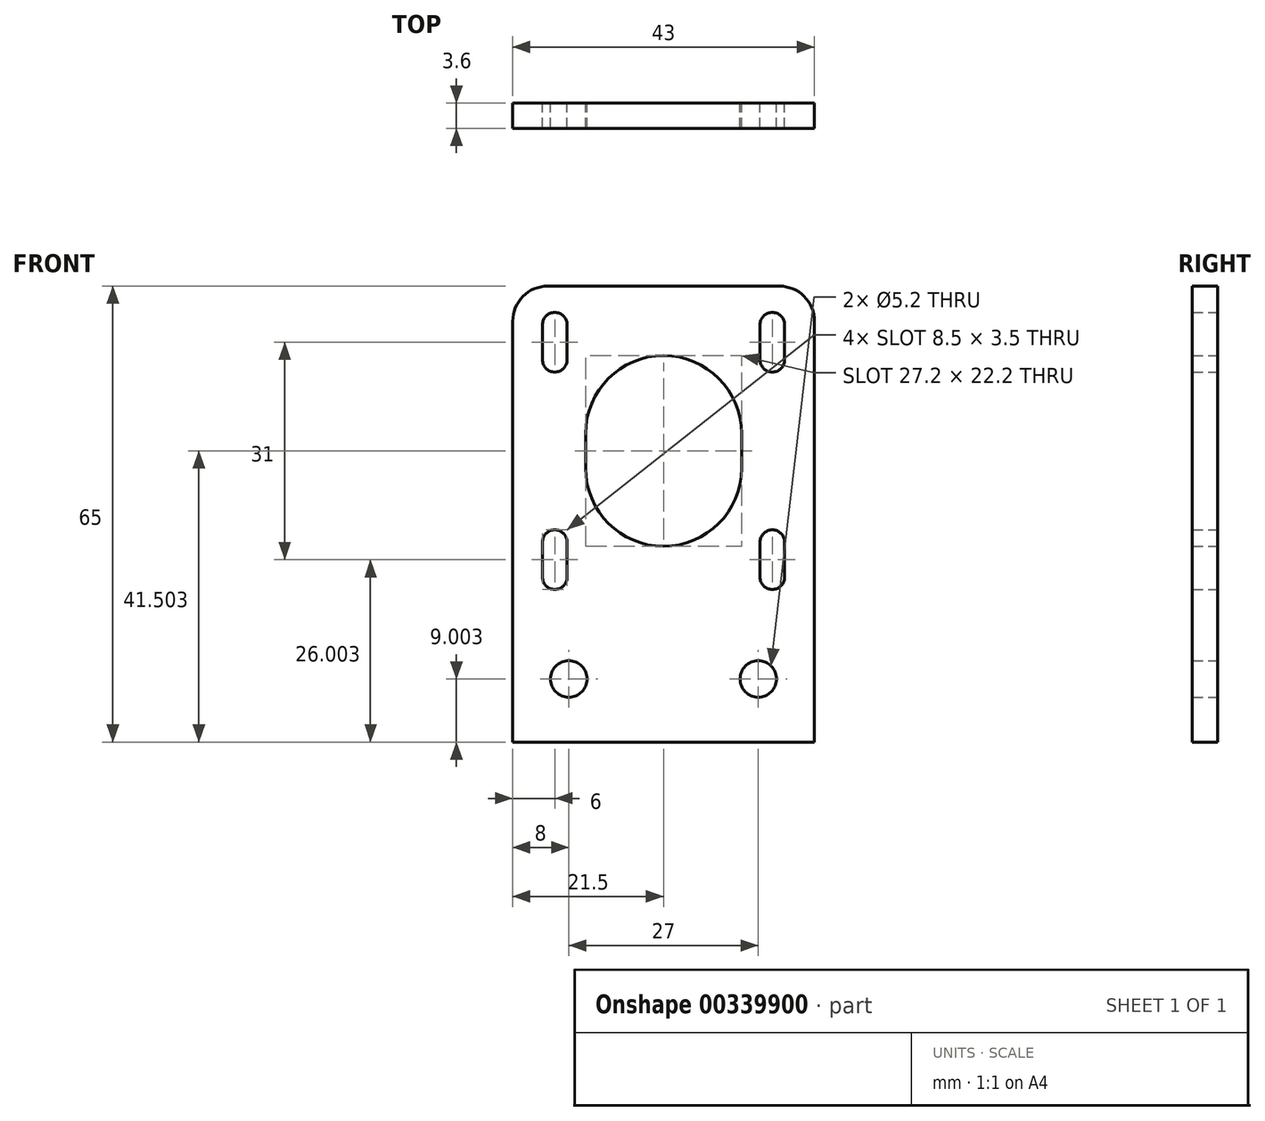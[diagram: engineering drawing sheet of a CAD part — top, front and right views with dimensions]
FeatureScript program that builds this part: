
annotation { "Feature Type Name" : "Feature", "Feature Type Description" : "" }
export const myFeature = defineFeature(function(context is Context, id is Id, definition is map)
    precondition{}
    {
        {
            var Q0;
            Q0=qCreatedBy(makeId("Front.planeOp"),FACE);
            var sketch = newSketch(context, id + "F0", { "sketchPlane" : qUnion([Q0])});
            skLineSegment(sketch, "E0.bottom", {"start": v(-21.5, 27.25) * mm, "end": v(21.5, 27.25) * mm});
            skLineSegment(sketch, "E0.top", {"start": v(-21.5, -37.75) * mm, "end": v(21.5, -37.75) * mm});
            skLineSegment(sketch, "E0.left", {"start": v(-21.5, 27.25) * mm, "end": v(-21.5, -37.75) * mm});
            skLineSegment(sketch, "E0.right", {"start": v(21.5, 27.25) * mm, "end": v(21.5, -37.75) * mm});
            skLineSegment(sketch, "E1", {"start": v(-21.5, -19.75) * mm, "end": v(21.5, -19.75) * mm, "construction": true});
            skLineSegment(sketch, "E2", {"start": v(-21.5, -28.75) * mm, "end": v(21.5, -28.75) * mm, "construction": true});
            skLineSegment(sketch, "E3", {"start": v(-21.5, 1.25) * mm, "end": v(21.5, 1.25) * mm, "construction": true});
            skPoint(sketch, "E3.endSnap0", {"position": v(21.5, -5.25) * mm});
            skLineSegment(sketch, "E4", {"start": v(-21.5, 6.25) * mm, "end": v(21.5, 6.25) * mm, "construction": true});
            skLineSegment(sketch, "E5", {"start": v(0, 27.25) * mm, "end": v(0, -37.75) * mm, "construction": true});
            skPoint(sketch, "E5.endSnap0", {"position": v(0, -37.75) * mm});
            skCircle(sketch, "E6", {"center": v(0, 1.25) * mm, "radius": 11.1 * mm});
            skCircle(sketch, "E7", {"center": v(0, 6.25) * mm, "radius": 11.1 * mm});
            skLineSegment(sketch, "E8", {"start": v(11.1, 1.25) * mm, "end": v(11.1, 6.25) * mm});
            skLineSegment(sketch, "E9", {"start": v(-11.1, 6.25) * mm, "end": v(-11.1, 1.25) * mm});
            skLineSegment(sketch, "E10", {"start": v(-15.5, 27.25) * mm, "end": v(-15.5, -19.75) * mm, "construction": true});
            skLineSegment(sketch, "E11", {"start": v(15.5, 27.25) * mm, "end": v(15.5, -19.75) * mm, "construction": true});
            skLineSegment(sketch, "E12", {"start": v(-21.5, -9.25) * mm, "end": v(21.5, -9.25) * mm, "construction": true});
            skLineSegment(sketch, "E13", {"start": v(-21.5, 21.75) * mm, "end": v(21.5, 21.75) * mm, "construction": true});
            skCircle(sketch, "E14", {"center": v(-15.5, 21.75) * mm, "radius": 1.75 * mm});
            skCircle(sketch, "E15", {"center": v(15.5, 21.75) * mm, "radius": 1.75 * mm});
            skCircle(sketch, "E16", {"center": v(-15.5, -9.25) * mm, "radius": 1.75 * mm});
            skCircle(sketch, "E17", {"center": v(15.5, -9.25) * mm, "radius": 1.75 * mm});
            skCircle(sketch, "E18", {"center": v(-15.5, 16.75) * mm, "radius": 1.75 * mm});
            skCircle(sketch, "E19", {"center": v(15.5, 16.75) * mm, "radius": 1.75 * mm});
            skCircle(sketch, "E20", {"center": v(15.5, -14.25) * mm, "radius": 1.75 * mm});
            skCircle(sketch, "E21", {"center": v(-15.5, -14.25) * mm, "radius": 1.75 * mm});
            skLineSegment(sketch, "E22", {"start": v(-17.25, 21.75) * mm, "end": v(-17.25, 16.75) * mm});
            skLineSegment(sketch, "E23", {"start": v(-13.75, 21.75) * mm, "end": v(-13.75, 16.75) * mm});
            skLineSegment(sketch, "E24", {"start": v(13.75, 21.75) * mm, "end": v(13.75, 16.75) * mm});
            skLineSegment(sketch, "E25", {"start": v(17.25, 21.75) * mm, "end": v(17.25, 16.75) * mm});
            skLineSegment(sketch, "E26", {"start": v(-17.25, -9.25) * mm, "end": v(-17.25, -14.25) * mm});
            skLineSegment(sketch, "E27", {"start": v(-13.75, -9.25) * mm, "end": v(-13.75, -14.25) * mm});
            skLineSegment(sketch, "E28", {"start": v(13.75, -9.25) * mm, "end": v(13.75, -14.25) * mm});
            skLineSegment(sketch, "E29", {"start": v(17.25, -9.25) * mm, "end": v(17.25, -14.25) * mm});
            skCircle(sketch, "E30", {"center": v(-13.5, -28.75) * mm, "radius": 2.6 * mm});
            skCircle(sketch, "E31", {"center": v(13.5, -28.75) * mm, "radius": 2.6 * mm});
            skSolve(sketch);
        }
        {
            var Q0;
            Q0 = qSketchRegion(id + "F0", true);
            extrude(context, id + "F1", {"entities" : qUnion([Q0]), "offsetDistance" : 25 * mm, "depth" : 3.6 * mm});
        }
        {
            var Q0;
            Q0=makeQuery(id+"F1.opExtrude","SWEPT_EDGE",EDGE,{"disambiguationData":[OSD([sQuery(id+"F0.wireOp",EDGE,"E0.bottom"),sQuery(id+"F0.wireOp",EDGE,"E0.left")])]});
            var Q1;
            Q1=makeQuery(id+"F1.opExtrude","SWEPT_EDGE",EDGE,{"disambiguationData":[OSD([sQuery(id+"F0.wireOp",EDGE,"E0.bottom"),sQuery(id+"F0.wireOp",EDGE,"E0.right")])]});
            fillet(context, id + "F2", {"entities" : qUnion([Q0, Q1]), "radius" : 5 * mm, "tangentPropagation" : true, "allowEdgeOverflow" : false});
        }
    });
